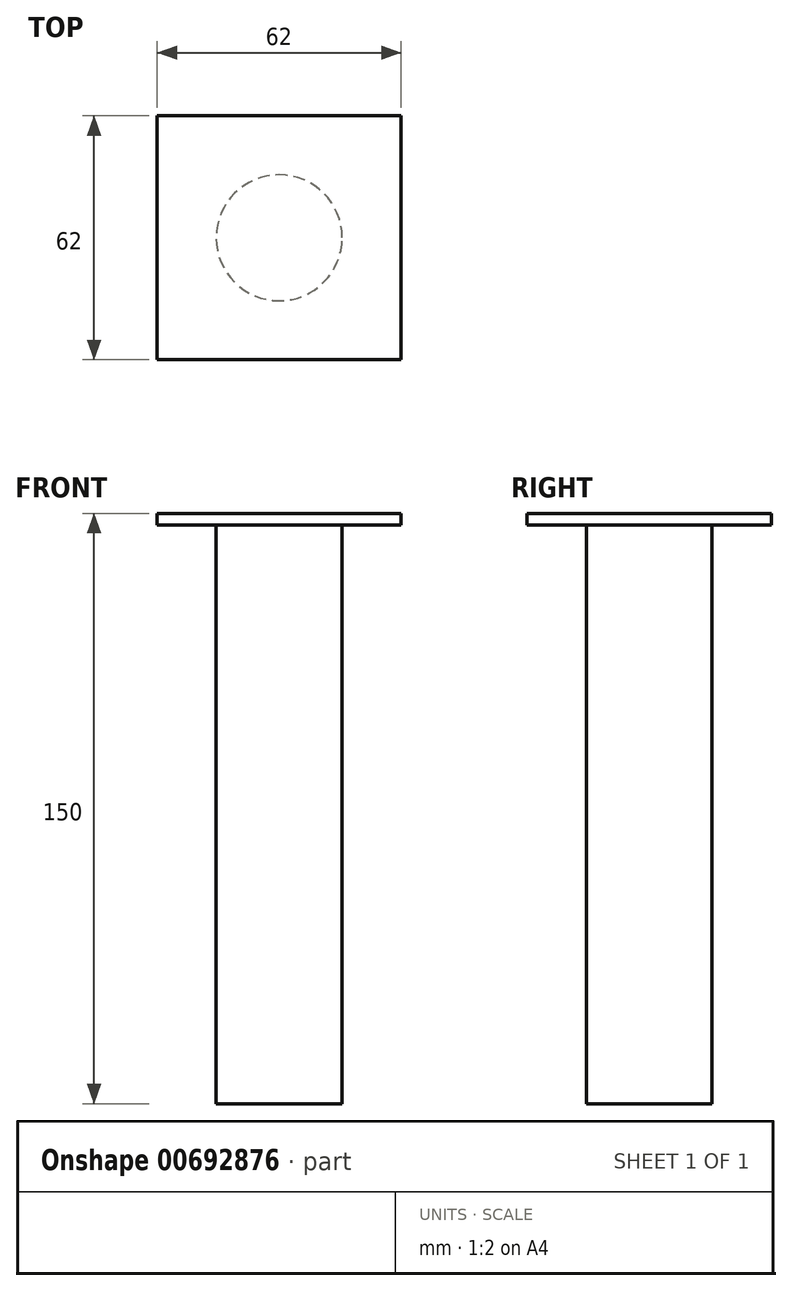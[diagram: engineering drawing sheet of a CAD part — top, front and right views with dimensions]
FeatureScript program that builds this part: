
annotation { "Feature Type Name" : "Feature", "Feature Type Description" : "" }
export const myFeature = defineFeature(function(context is Context, id is Id, definition is map)
    precondition{}
    {
        {
            var Q0;
            Q0=qCreatedBy(makeId("Top.planeOp"),FACE);
            var sketch = newSketch(context, id + "F0", { "sketchPlane" : qUnion([Q0])});
            skCircle(sketch, "E0", {"center": v(0, 0) * mm, "radius": 16 * mm});
            skSolve(sketch);
        }
        {
            var Q0;
            Q0 = qSketchRegion(id + "F0", true);
            extrude(context, id + "F1", {"entities" : qUnion([Q0]), "oppositeDirection" : true, "depth" : 150 * mm, "offsetDistance" : 25 * mm});
        }
        {
            var Q0;
            Q0=qCreatedBy(makeId("Top.planeOp"),FACE);
            var sketch = newSketch(context, id + "F2", { "sketchPlane" : qUnion([Q0])});
            skLineSegment(sketch, "E1.bottom", {"start": v(31, 31) * mm, "end": v(-31, 31) * mm});
            skLineSegment(sketch, "E1.top", {"start": v(31, -31) * mm, "end": v(-31, -31) * mm});
            skLineSegment(sketch, "E1.left", {"start": v(31, 31) * mm, "end": v(31, -31) * mm});
            skLineSegment(sketch, "E1.right", {"start": v(-31, 31) * mm, "end": v(-31, -31) * mm});
            skPoint(sketch, "E1.middle", {"position": v(0, 0) * mm});
            skSolve(sketch);
        }
        {
            var Q0;
            Q0 = qSketchRegion(id + "F2", true);
            extrude(context, id + "F3", {"entities" : qUnion([Q0]), "operationType" : NewBodyOperationType.ADD, "oppositeDirection" : true, "depth" : 3 * mm, "offsetDistance" : 25 * mm});
        }
    });
